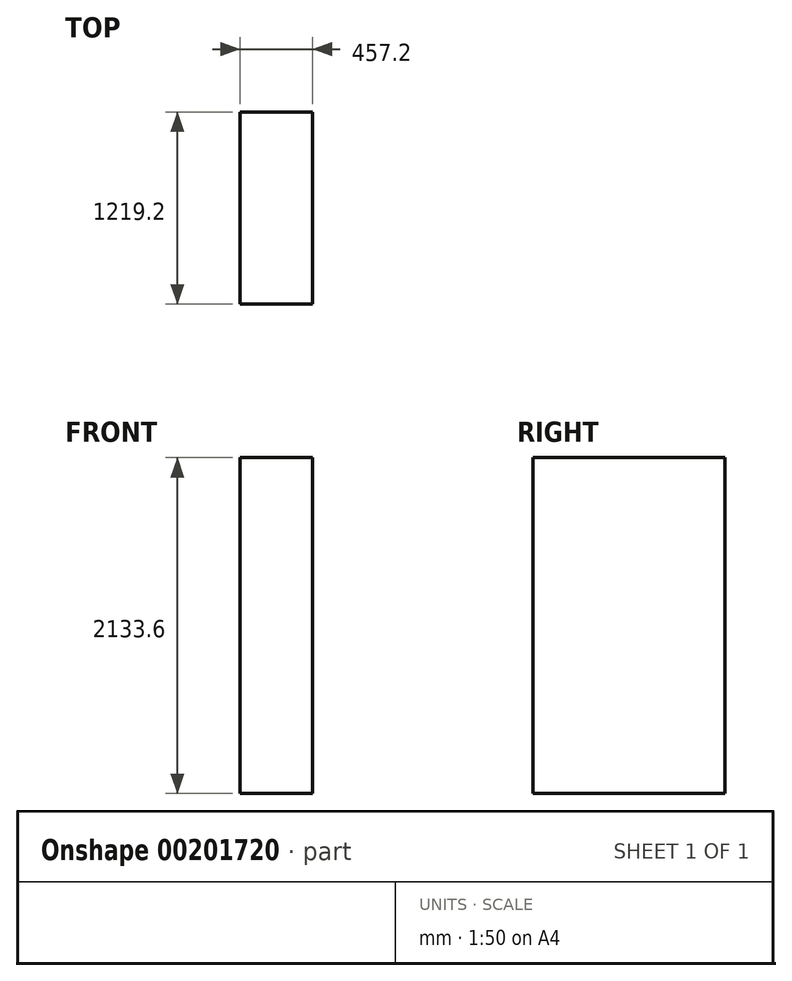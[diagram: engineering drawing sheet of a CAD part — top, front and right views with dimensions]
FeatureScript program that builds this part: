
annotation { "Feature Type Name" : "Feature", "Feature Type Description" : "" }
export const myFeature = defineFeature(function(context is Context, id is Id, definition is map)
    precondition{}
    {
        {
            var Q0;
            Q0=qCreatedBy(makeId("Top.planeOp"),FACE);
            var sketch = newSketch(context, id + "F0", { "sketchPlane" : qUnion([Q0])});
            skLineSegment(sketch, "E0.bottom", {"start": v(-228.6, 609.6) * mm, "end": v(228.6, 609.6) * mm});
            skLineSegment(sketch, "E0.top", {"start": v(-228.6, -609.6) * mm, "end": v(228.6, -609.6) * mm});
            skLineSegment(sketch, "E0.left", {"start": v(-228.6, 609.6) * mm, "end": v(-228.6, -609.6) * mm});
            skLineSegment(sketch, "E0.right", {"start": v(228.6, 609.6) * mm, "end": v(228.6, -609.6) * mm});
            skPoint(sketch, "E0.middle", {"position": v(0, 0) * mm});
            skSolve(sketch);
        }
        {
            var Q0;
            Q0=qSketchRegion(id+"F0",true);
            extrude(context, id + "F1", {"entities" : qUnion([Q0]), "depth" : 2133.6 * mm});
        }
    });
